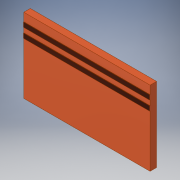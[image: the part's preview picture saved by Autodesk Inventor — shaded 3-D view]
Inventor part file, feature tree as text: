
AUTODESK INVENTOR PART (.ipt)
format: ipt  version: 2019 (Build 230136000, 136)  size: 189,952 bytes
history: native  units: mm
features: extrude x5, sketch x5, projected_geometry x4, fillet x2, pattern_linear x1
ambient origin geometry x8: Origin, YZ Plane, XZ Plane, XY Plane, X Axis, Y Axis, Z Axis, Center Point
bodies: Volumenkörper1 (feature_tree)
feature tree (17):
  extrude  "Extrusion1"  Depth=19.5mm
  extrude  "Extrusion2"  Depth=1.2mm
  pattern_linear  "Rechteckige Anordnung1"  Count1=13 Spacing1=33.0mm
  extrude  "Extrusion3"  Depth=2.15mm
  extrude  "Extrusion4"  Depth=0.1mm TaperAngle=0.0deg
  fillet  "Rundung1"  Radius=7.0mm
  extrude  "Extrusion5"  Depth=2.15mm
  fillet  "Rundung2"  Radius=4.0mm
  sketch  "Skizze7"  dims[d14=0.1mm d15=0.0mm d16=130.0mm d18=33.0mm d19=50.0mm d20=0.1mm d21=0.0mm d22=7.0mm d23=0.0mm d24=2.0mm d25=4.0mm d26=7.0mm d27=0.0mm d28=2.0mm d29=20.0mm d30=1.3mm d31=1.2mm d32=1.2mm d33=2.15mm]
  sketch  "Skizze1"  dims[d0=33.0mm d1=19.5mm]
  projected_geometry  "Projizierte Kontur1"
  sketch  "Skizze4"  dims[d8=1.7mm d9=0.0mm d10=1.2mm]
  projected_geometry  "Projizierte Kontur2"
  sketch  "Skizze5"  dims[d11=1.2mm]
  projected_geometry  "Projizierte Kontur3"
  sketch  "Skizze6"  dims[d12=1.3mm]
  projected_geometry  "Projizierte Kontur4"
